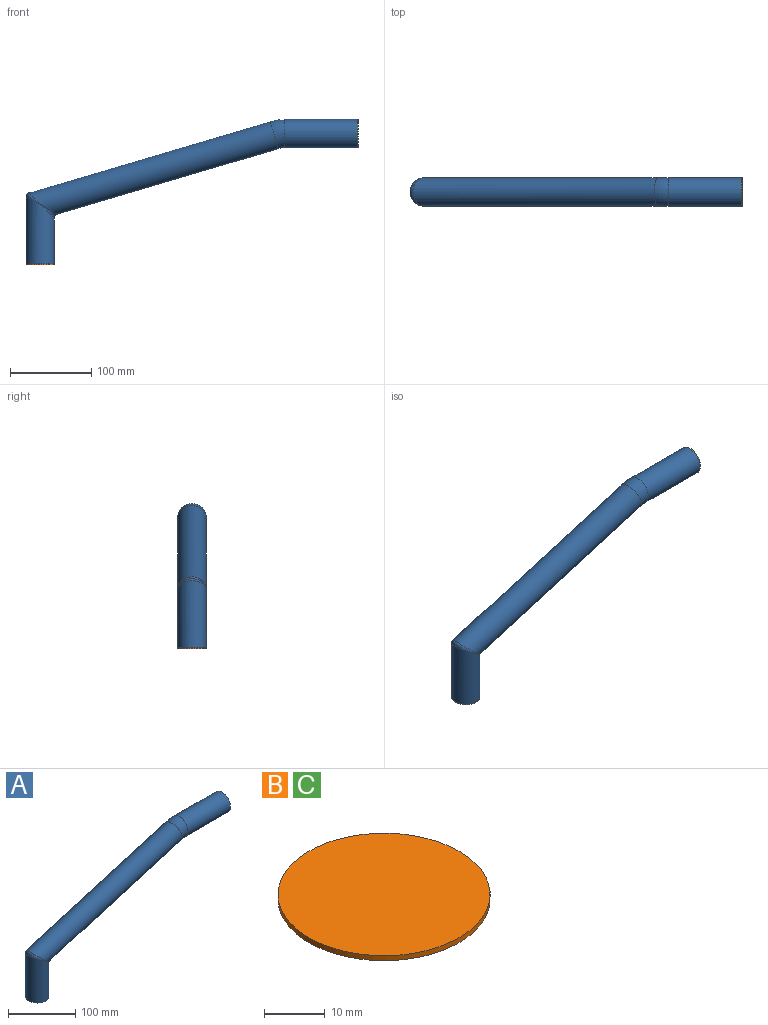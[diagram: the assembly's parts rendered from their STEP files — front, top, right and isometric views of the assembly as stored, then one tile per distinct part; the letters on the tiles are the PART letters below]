
ASSEMBLY  parts=3 mates=1
PART A: 13 faces, bbox 407.5x34.9x178.1 mm
  f0: cylinder r=15.99mm len=308.36mm, axis (0.96,0,0.28), area 30157.1mm2, adj f1,f12
  f1: torus R=42.86mm, axis (0,1,0), area 1239.2mm2, adj f0,f2
  f2: cylinder r=15.99mm len=90mm, axis (1,0,0), area 9041.7mm2, adj f1,f3
  f3: plane 34.93x34.93mm, normal (1,0,0), area 154.8mm2, adj f2,f4
  f4: cylinder r=17.46mm len=90mm, axis (1,0,0), area 9874.8mm2, adj f3,f5
  f5: torus R=42.86mm, axis (0,1,0), area 1353.3mm2, adj f4,f6
  f6: cylinder r=17.46mm len=306.7mm, axis (0.96,0,0.28), area 32674.8mm2, adj f5,f7,f10,f11
  f7: bspline ~34.93x17.46mm, area 233.4mm2, adj f6,f8
  f8: cylinder r=17.46mm len=82.38mm, axis (0,0,1), area 7753.4mm2, adj f7,f9,f10,f11
  f9: plane 34.93x34.93mm, normal (0,0,-1), area 154.8mm2, adj f8,f12
  f10: bspline ~15.37x12.25mm, area 13.9mm2, adj f6,f8
  f11: bspline ~31.32x21.04mm, area 115.6mm2, adj f6,f8
  f12: cylinder r=15.99mm len=84.99mm, axis (0,0,1), area 7338.1mm2, adj f0,f9
PART B: 3 faces, bbox 34.9x34.9x1 mm
  f0: cylinder r=17.46mm len=34.93mm, axis (0,0,1), area 109.7mm2, adj f1,f2
  f1: plane 34.93x34.93mm, normal (0,0,-1), area 958mm2, adj f0
  f2: plane 34.93x34.93mm, normal (0,0,1), area 958mm2, adj f0
PART C: same geometry as B
PLACE A at identity
PLACE B at identity
PLACE C rot(axis=(0.71,0,-0.71),180deg) t=(390,0,160)mm
MATE fastened C.f0 <-> A.f2  axis (-1,0,0) through (390,0,160)mm
